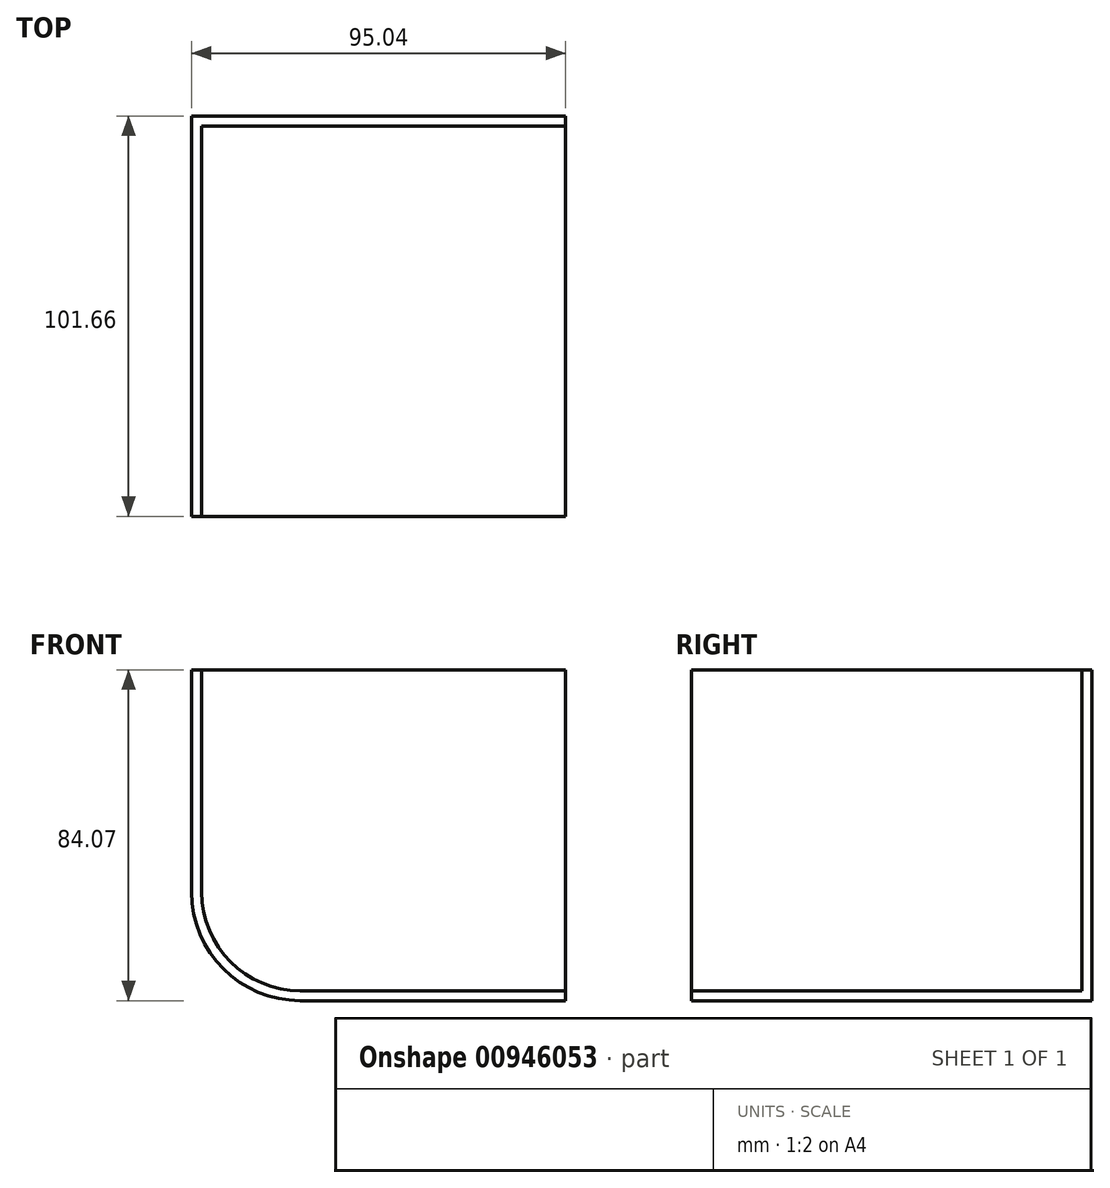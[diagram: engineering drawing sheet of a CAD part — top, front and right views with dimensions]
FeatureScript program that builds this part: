
annotation { "Feature Type Name" : "Feature", "Feature Type Description" : "" }
export const myFeature = defineFeature(function(context is Context, id is Id, definition is map)
    precondition{}
    {
        {
            var Q0;
            Q0=qCreatedBy(makeId("Top.planeOp"),FACE);
            var sketch = newSketch(context, id + "F0", { "sketchPlane" : qUnion([Q0])});
            skLineSegment(sketch, "E0.bottom", {"start": v(-47.52, 50.83) * mm, "end": v(47.52, 50.83) * mm});
            skLineSegment(sketch, "E0.top", {"start": v(-47.52, -50.83) * mm, "end": v(47.52, -50.83) * mm});
            skLineSegment(sketch, "E0.left", {"start": v(-47.52, 50.83) * mm, "end": v(-47.52, -50.83) * mm});
            skLineSegment(sketch, "E0.right", {"start": v(47.52, 50.83) * mm, "end": v(47.52, -50.83) * mm});
            skSolve(sketch);
        }
        {
            var Q0;
            Q0 = qSketchRegion(id + "F0", true);
            extrude(context, id + "F1", {"entities" : qUnion([Q0]), "depth" : 84.07 * mm, "offsetDistance" : 25.4 * mm});
        }
        {
            var Q0;
            Q0=makeQuery(id+"F1.opExtrude","CAP_EDGE",EDGE,{"disambiguationData":[OSD([sQuery(id+"F0.wireOp",EDGE,"E0.left")])],"isStart":true});
            fillet(context, id + "F2", {"entities" : qUnion([Q0]), "radius" : 27.6 * mm, "tangentPropagation" : true, "allowEdgeOverflow" : false});
        }
        {
            var Q0;
            Q0=makeQuery(id+"F1.opExtrude","SWEPT_FACE",FACE,{"disambiguationData":[OSD([sQuery(id+"F0.wireOp",EDGE,"E0.top")])]});
            var Q1;
            Q1=makeQuery(id+"F1.opExtrude","CAP_FACE",FACE,{"disambiguationData":[OSD([sQuery(id+"F0.wireOp",EDGE,"E0.bottom"),sQuery(id+"F0.wireOp",EDGE,"E0.top"),sQuery(id+"F0.wireOp",EDGE,"E0.left"),sQuery(id+"F0.wireOp",EDGE,"E0.right")])],"isStart":false});
            var Q2;
            Q2=makeQuery(id+"F1.opExtrude","SWEPT_FACE",FACE,{"disambiguationData":[OSD([sQuery(id+"F0.wireOp",EDGE,"E0.right")])]});
            shell(context, id + "F3", {"entities" : qUnion([Q0, Q1, Q2]), "thickness" : 2.54 * mm});
        }
    });
